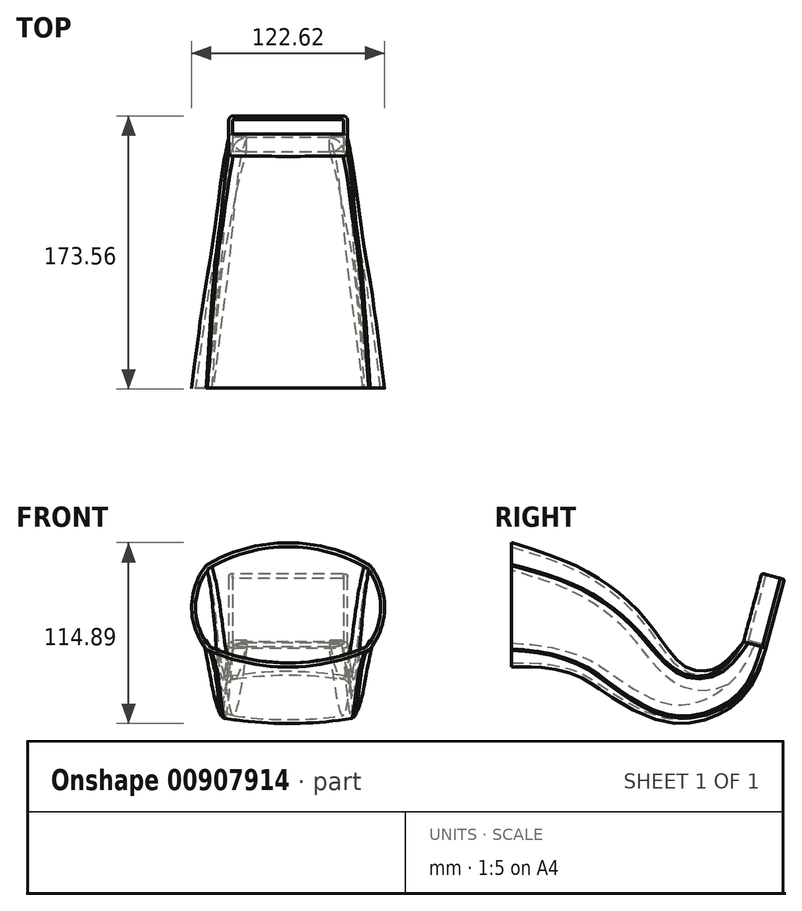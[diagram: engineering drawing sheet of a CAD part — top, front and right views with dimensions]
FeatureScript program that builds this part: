
annotation { "Feature Type Name" : "Feature", "Feature Type Description" : "" }
export const myFeature = defineFeature(function(context is Context, id is Id, definition is map)
    precondition{}
    {
        {
            var Q0;
            Q0=qCreatedBy(makeId("Right.planeOp"),FACE);
            var sketch = newSketch(context, id + "F0", { "sketchPlane" : qUnion([Q0])});
            skLineSegment(sketch, "E0", {"start": v(0, 0) * mm, "end": v(9.05, 33.77) * mm, "construction": true});
            skSolve(sketch);
        }
        {
            var Q0;
            Q0=sQuery(id+"F0.wireOp",EDGE,"E0");
            cPlane(context, id + "F1", {"entities" : qUnion([Q0]), "cplaneType" : CPlaneType.MID_PLANE, "offset" : 25 * mm, "width" : 150 * mm, "height" : 150 * mm});
        }
        {
            var Q0;
            Q0=qCreatedBy(id+"F1.planeOp",FACE);
            var sketch = newSketch(context, id + "F2", { "sketchPlane" : qUnion([Q0])});
            skLineSegment(sketch, "E1.bottom", {"start": v(35.25, 4.75) * mm, "end": v(-35.25, 4.75) * mm});
            skLineSegment(sketch, "E1.top", {"start": v(35.25, -4.75) * mm, "end": v(-35.25, -4.75) * mm});
            skLineSegment(sketch, "E1.left", {"start": v(35.25, 4.75) * mm, "end": v(35.25, -4.75) * mm});
            skLineSegment(sketch, "E1.right", {"start": v(-35.25, 4.75) * mm, "end": v(-35.25, -4.75) * mm});
            skLineSegment(sketch, "E2", {"start": v(35.25, 4.75) * mm, "end": v(-35.25, -4.75) * mm, "construction": true});
            skSolve(sketch);
        }
        {
            var Q0;
            Q0=qCreatedBy(makeId("Right.planeOp"),FACE);
            var sketch = newSketch(context, id + "F3", { "sketchPlane" : qUnion([Q0])});
            skPoint(sketch, "E3.0", {"position": v(4.52, 16.89) * mm});
            skFitSpline(sketch, "E4", {"points": [v(4.52, 16.89) * mm, v(-21.2, -13.25) * mm, v(-50.69, -13.25) * mm, v(-82.93, 11.56) * mm, v(-109.4, 29.2) * mm, v(-150, 40.77) * mm], "startDerivative": vector(-59.2, -227.9) * mm, "endDerivative": vector(-84.83, -3.64) * mm});
            skSolve(sketch);
        }
        {
            var Q0;
            Q0=qCreatedBy(makeId("Front.planeOp"),FACE);
            cPlane(context, id + "F4", {"entities" : qUnion([Q0]), "cplaneType" : CPlaneType.OFFSET, "offset" : 150 * mm, "width" : 150 * mm, "height" : 150 * mm});
        }
        {
            var Q0;
            Q0=qCreatedBy(id+"F4.planeOp",FACE);
            var sketch = newSketch(context, id + "F5", { "sketchPlane" : qUnion([Q0])});
            skLineSegment(sketch, "E5.bottom", {"start": v(-50, 65.77) * mm, "end": v(50, 65.77) * mm, "construction": true});
            skLineSegment(sketch, "E5.top", {"start": v(-50, 15.77) * mm, "end": v(50, 15.77) * mm, "construction": true});
            skLineSegment(sketch, "E5.left", {"start": v(-50, 65.77) * mm, "end": v(-50, 15.77) * mm, "construction": true});
            skLineSegment(sketch, "E5.right", {"start": v(50, 65.77) * mm, "end": v(50, 15.77) * mm, "construction": true});
            skLineSegment(sketch, "E6", {"start": v(-50, 65.77) * mm, "end": v(50, 15.77) * mm, "construction": true});
            skArc(sketch, "E7", {"start": v(50, 65.77) * mm, "mid": v(0, 79.17) * mm, "end": v(-50, 65.77) * mm});
            skArc(sketch, "E8", {"start": v(50, 15.77) * mm, "mid": v(58.78, 40.77) * mm, "end": v(50, 65.77) * mm});
            skArc(sketch, "E9", {"start": v(-50, 65.77) * mm, "mid": v(-58.78, 40.77) * mm, "end": v(-50, 15.77) * mm});
            skArc(sketch, "E10", {"start": v(-50, 15.77) * mm, "mid": v(0, 5.33) * mm, "end": v(50, 15.77) * mm});
            skSolve(sketch);
        }
        {
            var Q0;
            Q0=sQuery(id+"F3.wireOp",EDGE,"E4");
            var Q1;
            Q1=makeQuery(id+"F2.imprint","IMPRINT",FACE,{"disambiguationData":[TD([[makeQuery(id+"F2.imprint","IMPRINT",EDGE,{"derivedFrom":sQuery(id+"F2.wireOp",EDGE,"E1.bottom")}),1.0]])]});
            var Q2;
            Q2=makeQuery(id+"F5.imprint","IMPRINT",FACE,{"disambiguationData":[TD([[makeQuery(id+"F5.imprint","IMPRINT",EDGE,{"derivedFrom":sQuery(id+"F5.wireOp",EDGE,"E7")}),1.0]])]});
            loft(context, id + "F6", {"addSections" : true, "spine" : qUnion([Q0]), "sectionCount" : 5, "sheetProfilesArray" : [{ "sheetProfileEntities" : qUnion([Q1]) }, { "sheetProfileEntities" : qUnion([Q2]) }]});
        }
        {
            var Q0;
            Q0=makeQuery(id+"F6.opLoft","CAP_FACE",FACE,{"disambiguationData":[OSD([makeQuery(id+"F5.imprint","IMPRINT",FACE,{"disambiguationData":[TD([[makeQuery(id+"F5.imprint","IMPRINT",EDGE,{"derivedFrom":sQuery(id+"F5.wireOp",EDGE,"E7")}),1.0]])]})])],"isStart":true});
            var Q1;
            Q1=makeQuery(id+"F6.opLoft","CAP_FACE",FACE,{"disambiguationData":[OSD([makeQuery(id+"F2.imprint","IMPRINT",FACE,{"disambiguationData":[TD([[makeQuery(id+"F2.imprint","IMPRINT",EDGE,{"derivedFrom":sQuery(id+"F2.wireOp",EDGE,"E1.bottom")}),1.0]])]})])],"isStart":true});
            shell(context, id + "F7", {"entities" : qUnion([Q0, Q1]), "thickness" : 2.5 * mm, "oppositeDirection" : true});
        }
        {
            var Q0;
            Q0=makeQuery(id+"F6.opLoft","CAP_FACE",FACE,{"disambiguationData":[OSD([makeQuery(id+"F2.imprint","IMPRINT",FACE,{"disambiguationData":[TD([[makeQuery(id+"F2.imprint","IMPRINT",EDGE,{"derivedFrom":sQuery(id+"F2.wireOp",EDGE,"E1.bottom")}),1.0]])]})])],"isStart":true});
            var sketch = newSketch(context, id + "F8", { "sketchPlane" : qUnion([Q0])});
            skLineSegment(sketch, "E11.bottom", {"start": v(-35.25, -4.75) * mm, "end": v(-26.25, -4.75) * mm});
            skLineSegment(sketch, "E11.top", {"start": v(-35.25, 4.75) * mm, "end": v(-26.25, 4.75) * mm});
            skLineSegment(sketch, "E11.left", {"start": v(-35.25, -4.75) * mm, "end": v(-35.25, 4.75) * mm});
            skLineSegment(sketch, "E11.right", {"start": v(-26.25, -4.75) * mm, "end": v(-26.25, 4.75) * mm});
            skLineSegment(sketch, "E12.bottom", {"start": v(35.25, -4.75) * mm, "end": v(26.25, -4.75) * mm});
            skLineSegment(sketch, "E12.top", {"start": v(35.25, 4.75) * mm, "end": v(26.25, 4.75) * mm});
            skLineSegment(sketch, "E12.left", {"start": v(35.25, -4.75) * mm, "end": v(35.25, 4.75) * mm});
            skLineSegment(sketch, "E12.right", {"start": v(26.25, -4.75) * mm, "end": v(26.25, 4.75) * mm});
            skSolve(sketch);
        }
        {
            var Q0;
            Q0 = qSketchRegion(id + "F8", true);
            extrude(context, id + "F9", {"entities" : qUnion([Q0]), "depth" : 1.5 * mm, "offsetDistance" : 25 * mm});
        }
        {
            var Q0;
            Q0=makeQuery(id+"F6.opLoft","CAP_FACE",FACE,{"disambiguationData":[OSD([makeQuery(id+"F2.imprint","IMPRINT",FACE,{"disambiguationData":[TD([[makeQuery(id+"F2.imprint","IMPRINT",EDGE,{"derivedFrom":sQuery(id+"F2.wireOp",EDGE,"E1.bottom")}),1.0]])]})])],"isStart":true});
            extrude(context, id + "F10", {"entities" : qUnion([Q0]), "operationType" : NewBodyOperationType.ADD, "depth" : 45 * mm, "offsetDistance" : 25 * mm});
        }
        {
            var Q0;
            Q0=makeQuery(id+"F7.opShell","OFFSET_EDGE",EDGE,{"disambiguationData":[OSD([sQuery(id+"F2.wireOp",EDGE,"E1.top"),sQuery(id+"F2.wireOp",EDGE,"E1.right"),sQuery(id+"F5.wireOp",EDGE,"E7"),sQuery(id+"F5.wireOp",EDGE,"E9")])]});
            var Q1;
            Q1=makeQuery(id+"F7.opShell","OFFSET_EDGE",EDGE,{"disambiguationData":[OSD([sQuery(id+"F2.wireOp",EDGE,"E1.bottom"),sQuery(id+"F2.wireOp",EDGE,"E1.right"),sQuery(id+"F5.wireOp",EDGE,"E9"),sQuery(id+"F5.wireOp",EDGE,"E10")])]});
            var Q2;
            Q2=makeQuery(id+"F7.opShell","OFFSET_EDGE",EDGE,{"disambiguationData":[OSD([sQuery(id+"F2.wireOp",EDGE,"E1.top"),sQuery(id+"F2.wireOp",EDGE,"E1.left"),sQuery(id+"F5.wireOp",EDGE,"E7"),sQuery(id+"F5.wireOp",EDGE,"E8")])]});
            var Q3;
            Q3=makeQuery(id+"F7.opShell","OFFSET_EDGE",EDGE,{"disambiguationData":[OSD([sQuery(id+"F2.wireOp",EDGE,"E1.bottom"),sQuery(id+"F2.wireOp",EDGE,"E1.left"),sQuery(id+"F5.wireOp",EDGE,"E8"),sQuery(id+"F5.wireOp",EDGE,"E10")])]});
            fillet(context, id + "F11", {"entities" : qUnion([Q0, Q1, Q2, Q3]), "radius" : 9 * mm, "tangentPropagation" : true, "allowEdgeOverflow" : false});
        }
        {
            var Q0;
            {var subQ0=sQuery(id+"F2.wireOp",EDGE,"E1.left");var subQ1=sQuery(id+"F2.wireOp",EDGE,"E1.top");Q0=makeQuery(id+"F10.opExtrude","SWEPT_EDGE",EDGE,{"disambiguationData":[OSD([subQ1,subQ0]),TDD([makeQuery(id+"F6.opLoft","MID_CAP_VERTEX",VERTEX,{"disambiguationData":[OSD([subQ1,subQ0])],"capPos":0.0})])]});}
            var Q1;
            {var subQ0=sQuery(id+"F2.wireOp",EDGE,"E1.right");var subQ1=sQuery(id+"F2.wireOp",EDGE,"E1.top");Q1=makeQuery(id+"F10.opExtrude","SWEPT_EDGE",EDGE,{"disambiguationData":[OSD([subQ1,subQ0]),TDD([makeQuery(id+"F6.opLoft","MID_CAP_VERTEX",VERTEX,{"disambiguationData":[OSD([subQ1,subQ0])],"capPos":0.0})])]});}
            var Q2;
            {var subQ0=sQuery(id+"F2.wireOp",EDGE,"E1.right");var subQ1=sQuery(id+"F2.wireOp",EDGE,"E1.bottom");Q2=makeQuery(id+"F10.opExtrude","SWEPT_EDGE",EDGE,{"disambiguationData":[OSD([subQ1,subQ0]),TDD([makeQuery(id+"F6.opLoft","MID_CAP_VERTEX",VERTEX,{"disambiguationData":[OSD([subQ1,subQ0])],"capPos":0.0})])]});}
            var Q3;
            {var subQ0=sQuery(id+"F2.wireOp",EDGE,"E1.left");var subQ1=sQuery(id+"F2.wireOp",EDGE,"E1.bottom");Q3=makeQuery(id+"F10.opExtrude","SWEPT_EDGE",EDGE,{"disambiguationData":[OSD([subQ1,subQ0]),TDD([makeQuery(id+"F6.opLoft","MID_CAP_VERTEX",VERTEX,{"disambiguationData":[OSD([subQ1,subQ0])],"capPos":0.0})])]});}
            var Q4;
            Q4=makeQuery(id+"F6.opLoft","SWEPT_EDGE",EDGE,{"disambiguationData":[OSD([sQuery(id+"F2.wireOp",EDGE,"E1.top"),sQuery(id+"F2.wireOp",EDGE,"E1.left"),sQuery(id+"F5.wireOp",EDGE,"E7"),sQuery(id+"F5.wireOp",EDGE,"E8")])]});
            var Q5;
            Q5=makeQuery(id+"F6.opLoft","SWEPT_EDGE",EDGE,{"disambiguationData":[OSD([sQuery(id+"F2.wireOp",EDGE,"E1.top"),sQuery(id+"F2.wireOp",EDGE,"E1.right"),sQuery(id+"F5.wireOp",EDGE,"E7"),sQuery(id+"F5.wireOp",EDGE,"E9")])]});
            var Q6;
            Q6=makeQuery(id+"F6.opLoft","SWEPT_EDGE",EDGE,{"disambiguationData":[OSD([sQuery(id+"F2.wireOp",EDGE,"E1.bottom"),sQuery(id+"F2.wireOp",EDGE,"E1.right"),sQuery(id+"F5.wireOp",EDGE,"E9"),sQuery(id+"F5.wireOp",EDGE,"E10")])]});
            var Q7;
            Q7=makeQuery(id+"F6.opLoft","SWEPT_EDGE",EDGE,{"disambiguationData":[OSD([sQuery(id+"F2.wireOp",EDGE,"E1.bottom"),sQuery(id+"F2.wireOp",EDGE,"E1.left"),sQuery(id+"F5.wireOp",EDGE,"E8"),sQuery(id+"F5.wireOp",EDGE,"E10")])]});
            fillet(context, id + "F12", {"entities" : qUnion([Q0, Q1, Q2, Q3, Q4, Q5, Q6, Q7]), "radius" : 3 * mm, "tangentPropagation" : true, "allowEdgeOverflow" : false});
        }
        {
            var Q0;
            {var subQ0=sQuery(id+"F2.wireOp",EDGE,"E1.right");var subQ1=sQuery(id+"F2.wireOp",EDGE,"E1.top");Q0=makeQuery(id+"F10.opExtrude","SWEPT_EDGE",EDGE,{"disambiguationData":[OSD([subQ1,subQ0]),TDD([makeQuery(id+"F7.opShell","OFFSET_VERTEX",VERTEX,{"disambiguationData":[OSD([subQ1,subQ0])]})])]});}
            var Q1;
            {var subQ0=sQuery(id+"F2.wireOp",EDGE,"E1.right");var subQ1=sQuery(id+"F2.wireOp",EDGE,"E1.bottom");Q1=makeQuery(id+"F10.opExtrude","SWEPT_EDGE",EDGE,{"disambiguationData":[OSD([subQ1,subQ0]),TDD([makeQuery(id+"F7.opShell","OFFSET_VERTEX",VERTEX,{"disambiguationData":[OSD([subQ1,subQ0])]})])]});}
            var Q2;
            {var subQ0=sQuery(id+"F2.wireOp",EDGE,"E1.left");var subQ1=sQuery(id+"F2.wireOp",EDGE,"E1.bottom");Q2=makeQuery(id+"F10.opExtrude","SWEPT_EDGE",EDGE,{"disambiguationData":[OSD([subQ1,subQ0]),TDD([makeQuery(id+"F7.opShell","OFFSET_VERTEX",VERTEX,{"disambiguationData":[OSD([subQ1,subQ0])]})])]});}
            var Q3;
            {var subQ0=sQuery(id+"F2.wireOp",EDGE,"E1.left");var subQ1=sQuery(id+"F2.wireOp",EDGE,"E1.top");Q3=makeQuery(id+"F10.opExtrude","SWEPT_EDGE",EDGE,{"disambiguationData":[OSD([subQ1,subQ0]),TDD([makeQuery(id+"F7.opShell","OFFSET_VERTEX",VERTEX,{"disambiguationData":[OSD([subQ1,subQ0])]})])]});}
            var Q4;
            {var subQ0=sQuery(id+"F2.wireOp",EDGE,"E1.right");var subQ1=sQuery(id+"F2.wireOp",EDGE,"E1.left");var subQ2=sQuery(id+"F2.wireOp",EDGE,"E1.top");Q4=makeQuery(id+"F10.opExtrude","CAP_EDGE",EDGE,{"disambiguationData":[OSD([subQ2,subQ1,subQ0]),TDD([makeQuery(id+"F7.opShell","OFFSET_EDGE",EDGE,{"disambiguationData":[OSD([subQ2,subQ1,subQ0])]})])],"isStart":false});}
            var Q5;
            {var subQ0=sQuery(id+"F2.wireOp",EDGE,"E1.right");var subQ1=sQuery(id+"F2.wireOp",EDGE,"E1.left");var subQ2=sQuery(id+"F2.wireOp",EDGE,"E1.bottom");Q5=makeQuery(id+"F10.opExtrude","CAP_EDGE",EDGE,{"disambiguationData":[OSD([subQ2,subQ1,subQ0]),TDD([makeQuery(id+"F6.opLoft","MID_CAP_EDGE",EDGE,{"disambiguationData":[OSD([subQ2,subQ1,subQ0])],"capPos":0.0})])],"isStart":false});}
            fillet(context, id + "F13", {"entities" : qUnion([Q0, Q1, Q2, Q3, Q4, Q5]), "radius" : 1 * mm, "tangentPropagation" : true, "allowEdgeOverflow" : false});
        }
    });
